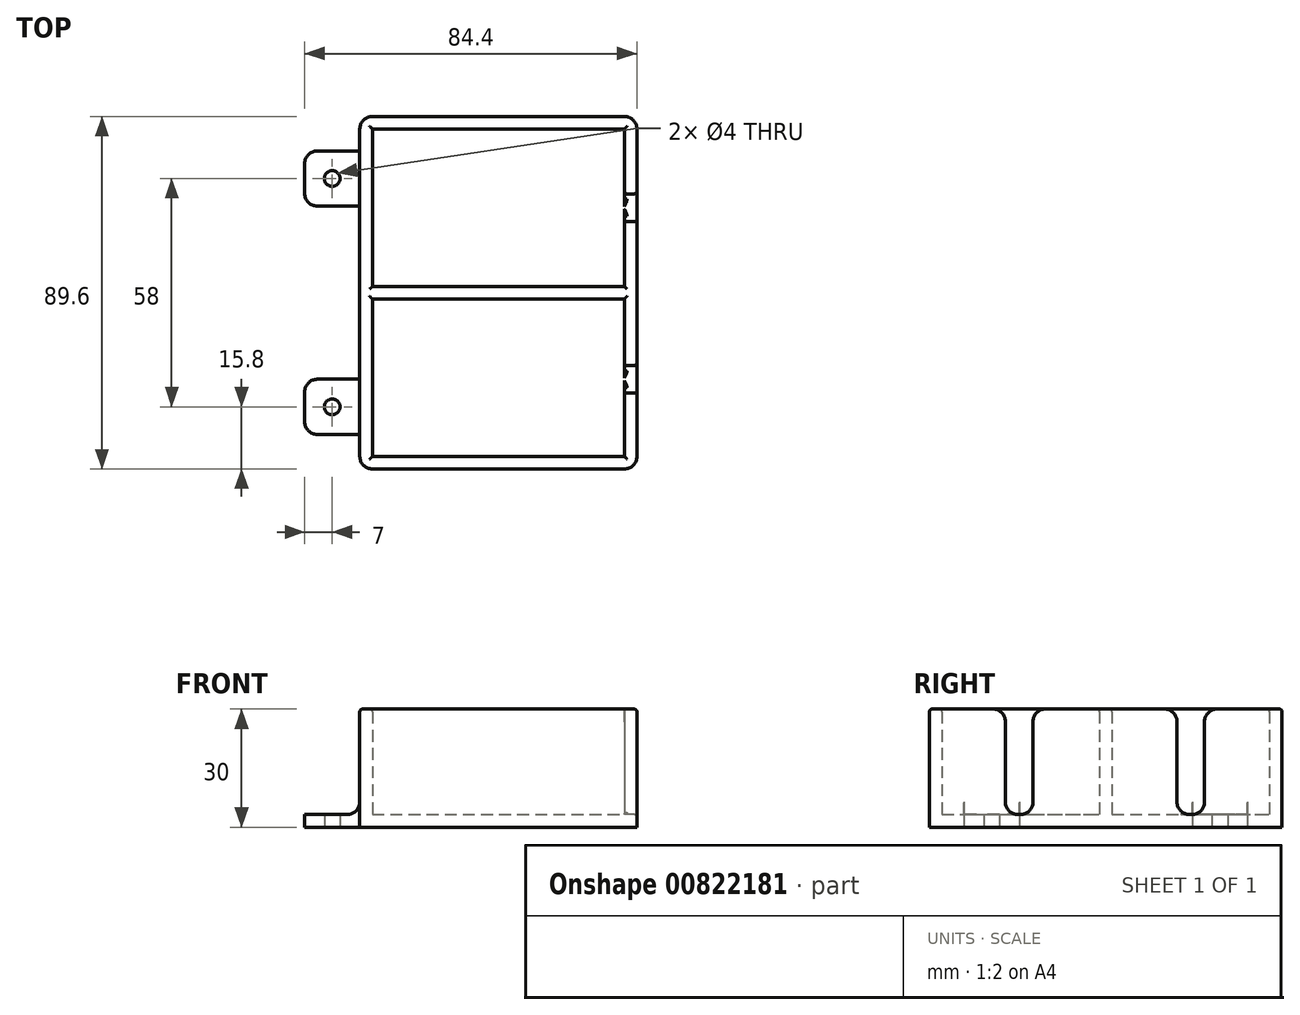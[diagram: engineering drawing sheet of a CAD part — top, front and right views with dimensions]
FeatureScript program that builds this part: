
annotation { "Feature Type Name" : "Feature", "Feature Type Description" : "" }
export const myFeature = defineFeature(function(context is Context, id is Id, definition is map)
    precondition{}
    {
        {
            var Q0;
            Q0=qCreatedBy(makeId("Top.planeOp"),FACE);
            var sketch = newSketch(context, id + "F0", { "sketchPlane" : qUnion([Q0])});
            skLineSegment(sketch, "E0.bottom", {"start": v(32, 20.4) * mm, "end": v(-32, 20.4) * mm});
            skLineSegment(sketch, "E0.top", {"start": v(32, -19.6) * mm, "end": v(-32, -19.6) * mm});
            skLineSegment(sketch, "E0.left", {"start": v(32, 20.4) * mm, "end": v(32, -19.6) * mm});
            skLineSegment(sketch, "E0.right", {"start": v(-32, 20.4) * mm, "end": v(-32, -19.6) * mm});
            skPoint(sketch, "E0.middle", {"position": v(0, 0) * mm});
            skLineSegment(sketch, "E1.bottom", {"start": v(35.2, 66.8) * mm, "end": v(-35.2, 66.8) * mm});
            skLineSegment(sketch, "E1.top", {"start": v(35.2, -22.8) * mm, "end": v(-35.2, -22.8) * mm});
            skLineSegment(sketch, "E1.left", {"start": v(35.2, 66.8) * mm, "end": v(35.2, -22.8) * mm});
            skLineSegment(sketch, "E1.right", {"start": v(-35.2, 66.8) * mm, "end": v(-35.2, 58) * mm});
            skLineSegment(sketch, "E2", {"start": v(32, 3.5) * mm, "end": v(35.2, 3.5) * mm});
            skLineSegment(sketch, "E3", {"start": v(32, -3.5) * mm, "end": v(35.2, -3.5) * mm});
            skLineSegment(sketch, "E4.bottom", {"start": v(32, 63.6) * mm, "end": v(-32, 63.6) * mm});
            skLineSegment(sketch, "E4.top", {"start": v(32, 23.6) * mm, "end": v(-32, 23.6) * mm});
            skLineSegment(sketch, "E4.left", {"start": v(32, 63.6) * mm, "end": v(32, 23.6) * mm});
            skLineSegment(sketch, "E4.right", {"start": v(-32, 63.6) * mm, "end": v(-32, 23.6) * mm});
            skLineSegment(sketch, "E5", {"start": v(32, 47.1) * mm, "end": v(35.2, 47.1) * mm});
            skLineSegment(sketch, "E6", {"start": v(32, 40.1) * mm, "end": v(35.2, 40.1) * mm});
            skCircle(sketch, "E7", {"center": v(-42.2, 51) * mm, "radius": 2 * mm});
            skCircle(sketch, "E8", {"center": v(-42.2, -7) * mm, "radius": 2 * mm});
            skLineSegment(sketch, "E9.bottom", {"start": v(-35.2, 58) * mm, "end": v(-49.2, 58) * mm});
            skLineSegment(sketch, "E9.top", {"start": v(-35.2, 44) * mm, "end": v(-49.2, 44) * mm});
            skLineSegment(sketch, "E9.right", {"start": v(-49.2, 58) * mm, "end": v(-49.2, 44) * mm});
            skLineSegment(sketch, "E10.bottom", {"start": v(-35.2, -14) * mm, "end": v(-49.2, -14) * mm});
            skLineSegment(sketch, "E10.top", {"start": v(-35.2, 0) * mm, "end": v(-49.2, 0) * mm});
            skLineSegment(sketch, "E10.right", {"start": v(-49.2, -14) * mm, "end": v(-49.2, 0) * mm});
            skLineSegment(sketch, "E11.trimOffspring", {"start": v(-35.2, 44) * mm, "end": v(-35.2, 0) * mm});
            skLineSegment(sketch, "E12.trimOffspring", {"start": v(-35.2, -14) * mm, "end": v(-35.2, -22.8) * mm});
            skLineSegment(sketch, "E13", {"start": v(-35.2, -14) * mm, "end": v(-35.2, 0) * mm});
            skLineSegment(sketch, "E14", {"start": v(-35.2, 44) * mm, "end": v(-35.2, 58) * mm});
            skLineSegment(sketch, "E15", {"start": v(-67.69, 22) * mm, "end": v(46.3, 22) * mm, "construction": true});
            skSolve(sketch);
        }
        {
            var Q0;
            {var subQ5=sQuery(id+"F0.wireOp",EDGE,"E0.bottom");Q0=makeQuery(id+"F0.imprint","IMPRINT",FACE,{"disambiguationData":[TD([[makeQuery(id+"F0.imprint","IMPRINT",EDGE,{"derivedFrom":subQ5}),-1.0]])]});}
            var Q1;
            {var subQ3=sQuery(id+"F0.wireOp",EDGE,"E0.bottom");Q1=makeQuery(id+"F0.imprint","IMPRINT",FACE,{"disambiguationData":[TD([[makeQuery(id+"F0.imprint","IMPRINT",EDGE,{"derivedFrom":subQ3}),1.0]])]});}
            var Q2;
            {var subQ0=sQuery(id+"F0.wireOp",EDGE,"E2");Q2=makeQuery(id+"F0.imprint","IMPRINT",FACE,{"disambiguationData":[TD([[makeQuery(id+"F0.imprint","IMPRINT",EDGE,{"derivedFrom":subQ0}),-1.0]])]});}
            var Q3;
            {var subQ3=sQuery(id+"F0.wireOp",EDGE,"E4.bottom");Q3=makeQuery(id+"F0.imprint","IMPRINT",FACE,{"disambiguationData":[TD([[makeQuery(id+"F0.imprint","IMPRINT",EDGE,{"derivedFrom":subQ3}),1.0]])]});}
            var Q4;
            {var subQ0=sQuery(id+"F0.wireOp",EDGE,"E5");Q4=makeQuery(id+"F0.imprint","IMPRINT",FACE,{"disambiguationData":[TD([[makeQuery(id+"F0.imprint","IMPRINT",EDGE,{"derivedFrom":subQ0}),-1.0]])]});}
            var Q5;
            Q5=makeQuery(id+"F0.imprint","IMPRINT",FACE,{"disambiguationData":[TD([[makeQuery(id+"F0.imprint","IMPRINT",EDGE,{"derivedFrom":sQuery(id+"F0.wireOp",EDGE,"E8")}),-1.0]])]});
            var Q6;
            Q6=makeQuery(id+"F0.imprint","IMPRINT",FACE,{"disambiguationData":[TD([[makeQuery(id+"F0.imprint","IMPRINT",EDGE,{"derivedFrom":sQuery(id+"F0.wireOp",EDGE,"E7")}),-1.0]])]});
            extrude(context, id + "F1", {"entities" : qUnion([Q0, Q1, Q2, Q3, Q4, Q5, Q6]), "depth" : 3.2 * mm, "offsetDistance" : 25 * mm});
        }
        {
            var Q0;
            {var subQ5=sQuery(id+"F0.wireOp",EDGE,"E0.bottom");Q0=makeQuery(id+"F0.imprint","IMPRINT",FACE,{"disambiguationData":[TD([[makeQuery(id+"F0.imprint","IMPRINT",EDGE,{"derivedFrom":subQ5}),-1.0]])]});}
            extrude(context, id + "F2", {"entities" : qUnion([Q0]), "operationType" : NewBodyOperationType.ADD, "depth" : 30 * mm, "offsetDistance" : 25 * mm});
        }
        {
            var Q0;
            {var subQ0=sQuery(id+"F0.wireOp",EDGE,"E1.right");var subQ1=sQuery(id+"F0.wireOp",EDGE,"E1.top");Q0=makeQuery(id+"F2.boolean.opBoolean","MERGE",EDGE,{"derivedFrom":[makeQuery(id+"F1.opExtrude","SWEPT_EDGE",EDGE,{"disambiguationData":[OSD([subQ1,subQ0])]}),makeQuery(id+"F2.opExtrude","SWEPT_EDGE",EDGE,{"disambiguationData":[OSD([subQ1,subQ0])]})]});}
            var Q1;
            {var subQ0=sQuery(id+"F0.wireOp",EDGE,"E1.right");var subQ1=sQuery(id+"F0.wireOp",EDGE,"E1.bottom");Q1=makeQuery(id+"F2.boolean.opBoolean","MERGE",EDGE,{"derivedFrom":[makeQuery(id+"F1.opExtrude","SWEPT_EDGE",EDGE,{"disambiguationData":[OSD([subQ1,subQ0])]}),makeQuery(id+"F2.opExtrude","SWEPT_EDGE",EDGE,{"disambiguationData":[OSD([subQ1,subQ0])]})]});}
            var Q2;
            {var subQ0=sQuery(id+"F0.wireOp",EDGE,"E1.left");var subQ1=sQuery(id+"F0.wireOp",EDGE,"E1.top");Q2=makeQuery(id+"F2.boolean.opBoolean","MERGE",EDGE,{"derivedFrom":[makeQuery(id+"F1.opExtrude","SWEPT_EDGE",EDGE,{"disambiguationData":[OSD([subQ1,subQ0])]}),makeQuery(id+"F2.opExtrude","SWEPT_EDGE",EDGE,{"disambiguationData":[OSD([subQ1,subQ0])]})]});}
            var Q3;
            {var subQ0=sQuery(id+"F0.wireOp",EDGE,"E1.left");var subQ1=sQuery(id+"F0.wireOp",EDGE,"E1.bottom");Q3=makeQuery(id+"F2.boolean.opBoolean","MERGE",EDGE,{"derivedFrom":[makeQuery(id+"F1.opExtrude","SWEPT_EDGE",EDGE,{"disambiguationData":[OSD([subQ1,subQ0])]}),makeQuery(id+"F2.opExtrude","SWEPT_EDGE",EDGE,{"disambiguationData":[OSD([subQ1,subQ0])]})]});}
            var Q4;
            Q4=makeQuery(id+"F2.boolean.opBoolean","INTERSECT",EDGE,{"derivedFrom":[makeQuery(id+"F1.opExtrude","CAP_FACE",FACE,{"disambiguationData":[OSD([sQuery(id+"F0.wireOp",EDGE,"E1.bottom"),sQuery(id+"F0.wireOp",EDGE,"E1.top"),sQuery(id+"F0.wireOp",EDGE,"E1.left"),sQuery(id+"F0.wireOp",EDGE,"E1.right")])],"isStart":false}),makeQuery(id+"F2.opExtrude","SWEPT_FACE",FACE,{"disambiguationData":[OSD([sQuery(id+"F0.wireOp",EDGE,"E3")])]})]});
            var Q5;
            Q5=makeQuery(id+"F2.boolean.opBoolean","INTERSECT",EDGE,{"derivedFrom":[makeQuery(id+"F1.opExtrude","CAP_FACE",FACE,{"disambiguationData":[OSD([sQuery(id+"F0.wireOp",EDGE,"E1.bottom"),sQuery(id+"F0.wireOp",EDGE,"E1.top"),sQuery(id+"F0.wireOp",EDGE,"E1.left"),sQuery(id+"F0.wireOp",EDGE,"E1.right")])],"isStart":false}),makeQuery(id+"F2.opExtrude","SWEPT_FACE",FACE,{"disambiguationData":[OSD([sQuery(id+"F0.wireOp",EDGE,"E2")])]})]});
            var Q6;
            Q6=makeQuery(id+"F2.opExtrude","CAP_EDGE",EDGE,{"disambiguationData":[OSD([sQuery(id+"F0.wireOp",EDGE,"E3")])],"isStart":false});
            var Q7;
            Q7=makeQuery(id+"F2.opExtrude","CAP_EDGE",EDGE,{"disambiguationData":[OSD([sQuery(id+"F0.wireOp",EDGE,"E2")])],"isStart":false});
            var Q8;
            Q8=makeQuery(id+"F2.boolean.opBoolean","INTERSECT",EDGE,{"derivedFrom":[makeQuery(id+"F1.opExtrude","CAP_FACE",FACE,{"disambiguationData":[OSD([sQuery(id+"F0.wireOp",EDGE,"E1.bottom"),sQuery(id+"F0.wireOp",EDGE,"E1.top"),sQuery(id+"F0.wireOp",EDGE,"E1.left"),sQuery(id+"F0.wireOp",EDGE,"E1.right")])],"isStart":false}),makeQuery(id+"F2.opExtrude","SWEPT_FACE",FACE,{"disambiguationData":[OSD([sQuery(id+"F0.wireOp",EDGE,"E6")])]})]});
            var Q9;
            Q9=makeQuery(id+"F2.opExtrude","CAP_EDGE",EDGE,{"disambiguationData":[OSD([sQuery(id+"F0.wireOp",EDGE,"E6")])],"isStart":false});
            var Q10;
            Q10=makeQuery(id+"F2.opExtrude","CAP_EDGE",EDGE,{"disambiguationData":[OSD([sQuery(id+"F0.wireOp",EDGE,"E5")])],"isStart":false});
            var Q11;
            Q11=makeQuery(id+"F2.boolean.opBoolean","INTERSECT",EDGE,{"derivedFrom":[makeQuery(id+"F1.opExtrude","CAP_FACE",FACE,{"disambiguationData":[OSD([sQuery(id+"F0.wireOp",EDGE,"E1.bottom"),sQuery(id+"F0.wireOp",EDGE,"E1.top"),sQuery(id+"F0.wireOp",EDGE,"E1.left"),sQuery(id+"F0.wireOp",EDGE,"E1.right")])],"isStart":false}),makeQuery(id+"F2.opExtrude","SWEPT_FACE",FACE,{"disambiguationData":[OSD([sQuery(id+"F0.wireOp",EDGE,"E5")])]})]});
            var Q12;
            Q12=makeQuery(id+"F1.opExtrude","SWEPT_EDGE",EDGE,{"disambiguationData":[OSD([sQuery(id+"F0.wireOp",EDGE,"E10.bottom"),sQuery(id+"F0.wireOp",EDGE,"E10.right")])]});
            var Q13;
            Q13=makeQuery(id+"F1.opExtrude","SWEPT_EDGE",EDGE,{"disambiguationData":[OSD([sQuery(id+"F0.wireOp",EDGE,"E10.top"),sQuery(id+"F0.wireOp",EDGE,"E10.right")])]});
            var Q14;
            Q14=makeQuery(id+"F1.opExtrude","SWEPT_EDGE",EDGE,{"disambiguationData":[OSD([sQuery(id+"F0.wireOp",EDGE,"E9.top"),sQuery(id+"F0.wireOp",EDGE,"E9.right")])]});
            var Q15;
            Q15=makeQuery(id+"F1.opExtrude","SWEPT_EDGE",EDGE,{"disambiguationData":[OSD([sQuery(id+"F0.wireOp",EDGE,"E9.bottom"),sQuery(id+"F0.wireOp",EDGE,"E9.right")])]});
            var Q16;
            {var subQ0=sQuery(id+"F0.wireOp",EDGE,"E12.trimOffspring");var subQ1=sQuery(id+"F0.wireOp",EDGE,"E11.trimOffspring");var subQ2=sQuery(id+"F0.wireOp",EDGE,"E1.right");Q16=makeQuery(id+"F2.boolean.opBoolean","INTERSECT",EDGE,{"disambiguationData":[OD(1.0)],"derivedFrom":[makeQuery(id+"F1.opExtrude","CAP_FACE",FACE,{"disambiguationData":[OSD([sQuery(id+"F0.wireOp",EDGE,"E1.bottom"),sQuery(id+"F0.wireOp",EDGE,"E1.top"),sQuery(id+"F0.wireOp",EDGE,"E1.left"),subQ2,sQuery(id+"F0.wireOp",EDGE,"E7"),sQuery(id+"F0.wireOp",EDGE,"E8"),sQuery(id+"F0.wireOp",EDGE,"E9.bottom"),sQuery(id+"F0.wireOp",EDGE,"E9.top"),sQuery(id+"F0.wireOp",EDGE,"E9.right"),sQuery(id+"F0.wireOp",EDGE,"E10.bottom"),sQuery(id+"F0.wireOp",EDGE,"E10.top"),sQuery(id+"F0.wireOp",EDGE,"E10.right"),subQ1,subQ0])],"isStart":false}),makeQuery(id+"F2.opExtrude","SWEPT_FACE",FACE,{"disambiguationData":[OSD([subQ2,subQ1,subQ0,sQuery(id+"F0.wireOp",EDGE,"E13"),sQuery(id+"F0.wireOp",EDGE,"E14")])]})]});}
            var Q17;
            {var subQ0=sQuery(id+"F0.wireOp",EDGE,"E12.trimOffspring");var subQ1=sQuery(id+"F0.wireOp",EDGE,"E11.trimOffspring");var subQ2=sQuery(id+"F0.wireOp",EDGE,"E1.right");Q17=makeQuery(id+"F2.boolean.opBoolean","INTERSECT",EDGE,{"disambiguationData":[OD(0.0)],"derivedFrom":[makeQuery(id+"F1.opExtrude","CAP_FACE",FACE,{"disambiguationData":[OSD([sQuery(id+"F0.wireOp",EDGE,"E1.bottom"),sQuery(id+"F0.wireOp",EDGE,"E1.top"),sQuery(id+"F0.wireOp",EDGE,"E1.left"),subQ2,sQuery(id+"F0.wireOp",EDGE,"E7"),sQuery(id+"F0.wireOp",EDGE,"E8"),sQuery(id+"F0.wireOp",EDGE,"E9.bottom"),sQuery(id+"F0.wireOp",EDGE,"E9.top"),sQuery(id+"F0.wireOp",EDGE,"E9.right"),sQuery(id+"F0.wireOp",EDGE,"E10.bottom"),sQuery(id+"F0.wireOp",EDGE,"E10.top"),sQuery(id+"F0.wireOp",EDGE,"E10.right"),subQ1,subQ0])],"isStart":false}),makeQuery(id+"F2.opExtrude","SWEPT_FACE",FACE,{"disambiguationData":[OSD([subQ2,subQ1,subQ0,sQuery(id+"F0.wireOp",EDGE,"E13"),sQuery(id+"F0.wireOp",EDGE,"E14")])]})]});}
            var Q18;
            Q18=makeQuery(id+"F1.opExtrude","SWEPT_EDGE",EDGE,{"disambiguationData":[OSD([sQuery(id+"F0.wireOp",EDGE,"E9.top"),sQuery(id+"F0.wireOp",EDGE,"E11.trimOffspring"),sQuery(id+"F0.wireOp",EDGE,"E14")])]});
            var Q19;
            Q19=makeQuery(id+"F1.opExtrude","SWEPT_EDGE",EDGE,{"disambiguationData":[OSD([sQuery(id+"F0.wireOp",EDGE,"E10.top"),sQuery(id+"F0.wireOp",EDGE,"E11.trimOffspring"),sQuery(id+"F0.wireOp",EDGE,"E13")])]});
            var Q20;
            Q20=makeQuery(id+"F1.opExtrude","SWEPT_EDGE",EDGE,{"disambiguationData":[OSD([sQuery(id+"F0.wireOp",EDGE,"E10.bottom"),sQuery(id+"F0.wireOp",EDGE,"E12.trimOffspring"),sQuery(id+"F0.wireOp",EDGE,"E13")])]});
            var Q21;
            Q21=makeQuery(id+"F1.opExtrude","SWEPT_EDGE",EDGE,{"disambiguationData":[OSD([sQuery(id+"F0.wireOp",EDGE,"E1.right"),sQuery(id+"F0.wireOp",EDGE,"E9.bottom"),sQuery(id+"F0.wireOp",EDGE,"E14")])]});
            fillet(context, id + "F3", {"entities" : qUnion([Q0, Q1, Q2, Q3, Q4, Q5, Q6, Q7, Q8, Q9, Q10, Q11, Q12, Q13, Q14, Q15, Q16, Q17, Q18, Q19, Q20, Q21]), "radius" : 3.2 * mm, "tangentPropagation" : true, "allowEdgeOverflow" : false});
        }
        {
            var Q0;
            Q0=makeQuery(id+"F2.opExtrude","CAP_FACE",FACE,{"disambiguationData":[OSD([sQuery(id+"F0.wireOp",EDGE,"E0.bottom"),sQuery(id+"F0.wireOp",EDGE,"E0.top"),sQuery(id+"F0.wireOp",EDGE,"E0.left"),sQuery(id+"F0.wireOp",EDGE,"E0.right"),sQuery(id+"F0.wireOp",EDGE,"E1.bottom"),sQuery(id+"F0.wireOp",EDGE,"E1.top"),sQuery(id+"F0.wireOp",EDGE,"E1.left"),sQuery(id+"F0.wireOp",EDGE,"E1.right"),sQuery(id+"F0.wireOp",EDGE,"E2"),sQuery(id+"F0.wireOp",EDGE,"E3")])],"isStart":false});
            fillet(context, id + "F4", {"entities" : qUnion([Q0]), "radius" : .7 * mm, "tangentPropagation" : true, "allowEdgeOverflow" : false});
        }
    });
